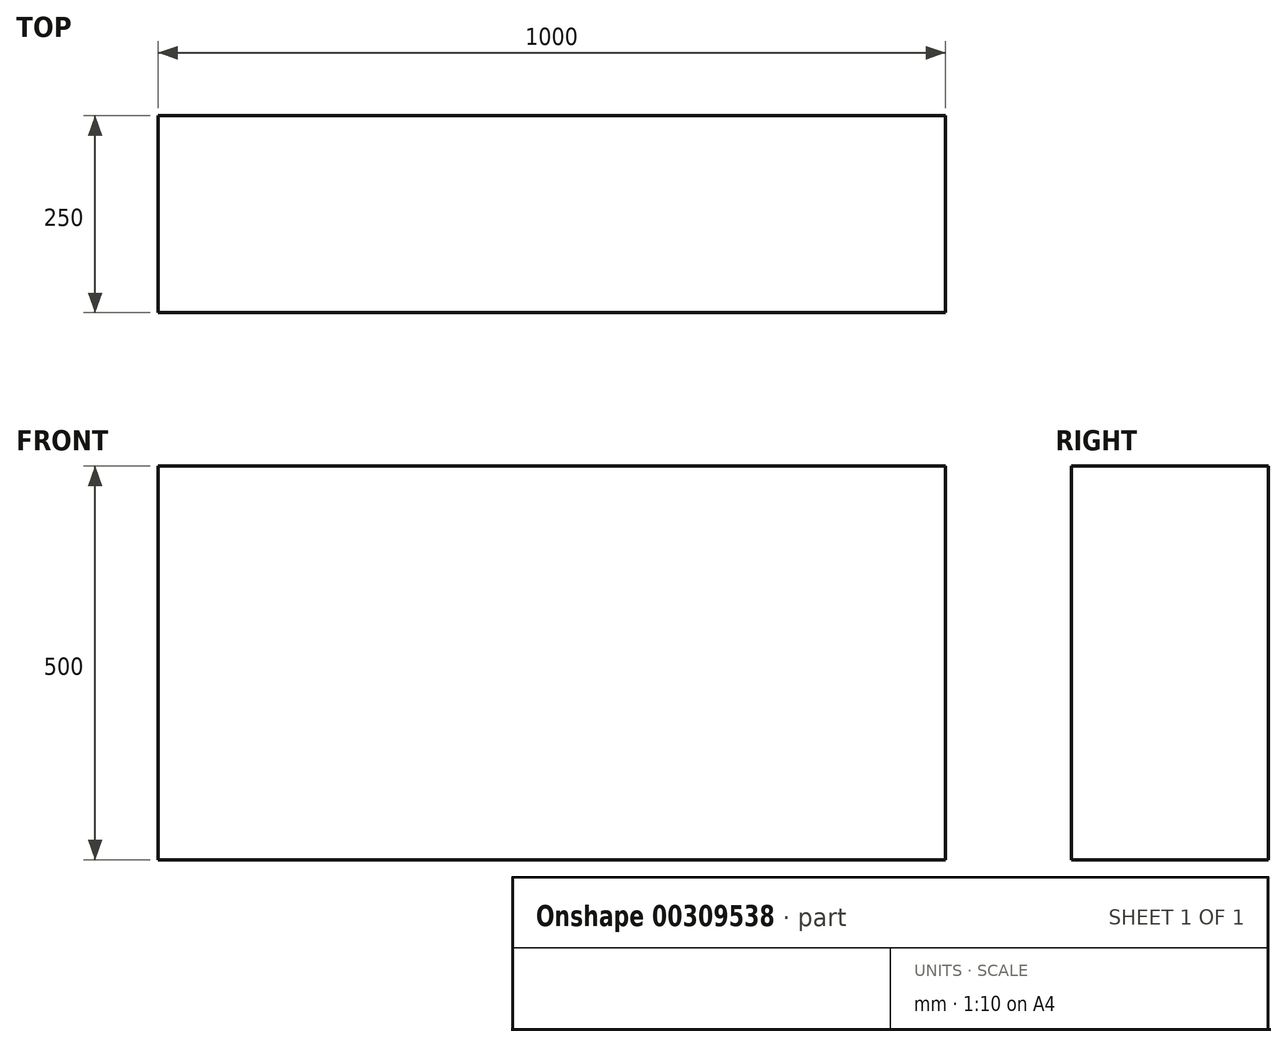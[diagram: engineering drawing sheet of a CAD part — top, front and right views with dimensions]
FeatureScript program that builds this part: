
annotation { "Feature Type Name" : "Feature", "Feature Type Description" : "" }
export const myFeature = defineFeature(function(context is Context, id is Id, definition is map)
    precondition{}
    {
        {
            var Q0;
            Q0=qCreatedBy(makeId("Front.planeOp"),FACE);
            var sketch = newSketch(context, id + "F0", { "sketchPlane" : qUnion([Q0])});
            skLineSegment(sketch, "E0.bottom", {"start": v(-510.76, 272.62) * mm, "end": v(489.24, 272.62) * mm});
            skLineSegment(sketch, "E0.top", {"start": v(-510.76, -227.38) * mm, "end": v(489.24, -227.38) * mm});
            skLineSegment(sketch, "E0.left", {"start": v(-510.76, 272.62) * mm, "end": v(-510.76, -227.38) * mm});
            skLineSegment(sketch, "E0.right", {"start": v(489.24, 272.62) * mm, "end": v(489.24, -227.38) * mm});
            skSolve(sketch);
        }
        {
            var Q0;
            Q0=makeQuery(id+"F0.imprint","IMPRINT",FACE,{"disambiguationData":[TD([[makeQuery(id+"F0.imprint","IMPRINT",EDGE,{"derivedFrom":sQuery(id+"F0.wireOp",EDGE,"E0.bottom")}),-1.0]])]});
            extrude(context, id + "F1", {"entities" : qUnion([Q0]), "depth" : 250 * mm});
        }
    });
